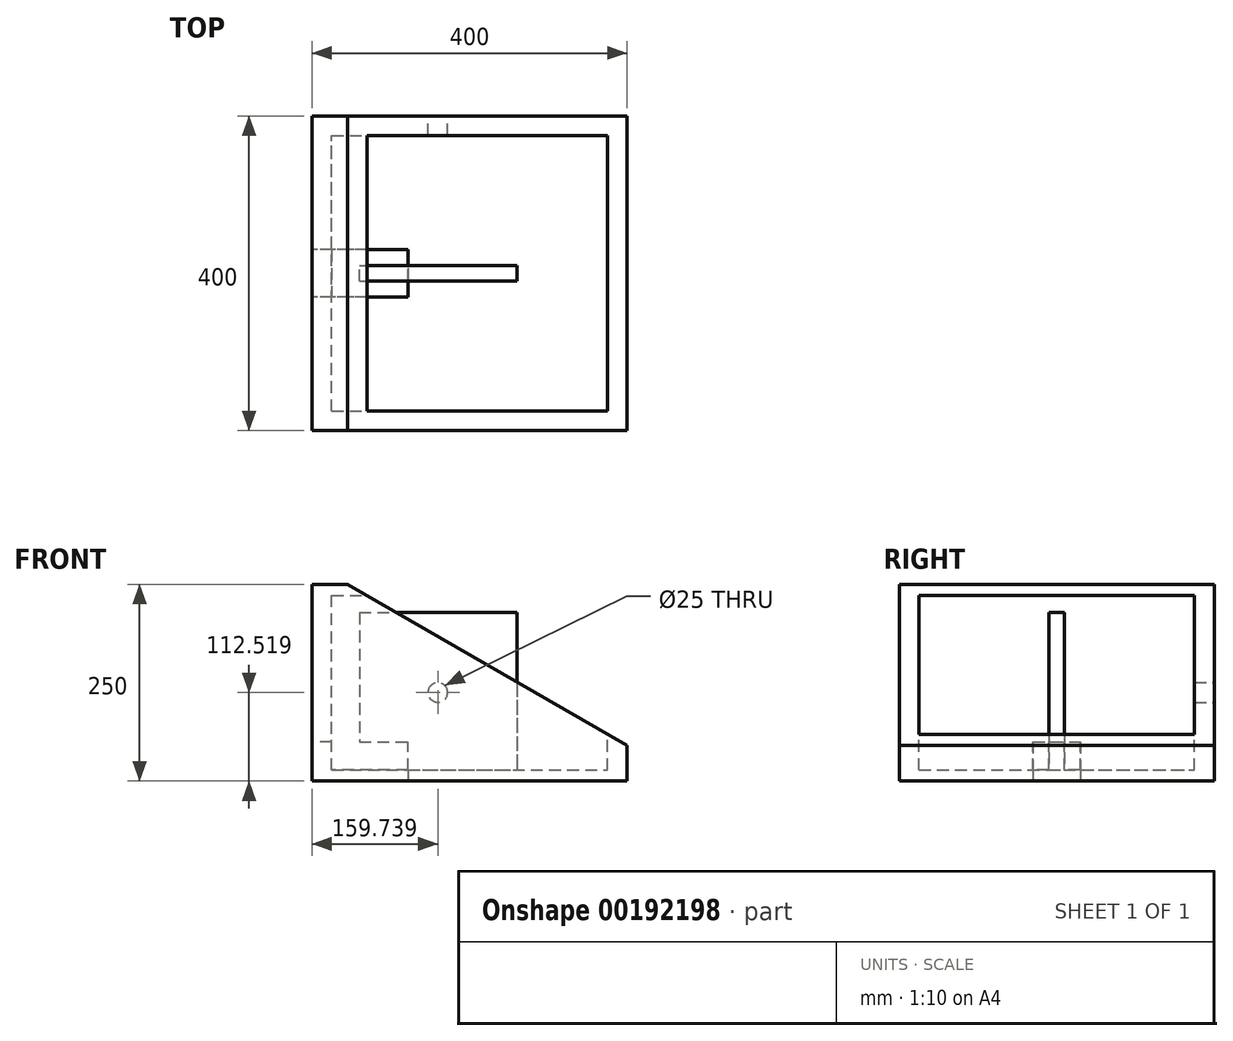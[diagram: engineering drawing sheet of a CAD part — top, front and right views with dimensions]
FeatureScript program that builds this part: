
annotation { "Feature Type Name" : "Feature", "Feature Type Description" : "" }
export const myFeature = defineFeature(function(context is Context, id is Id, definition is map)
    precondition{}
    {
        {
            var Q0;
            Q0=qCreatedBy(makeId("Front.planeOp"),FACE);
            var sketch = newSketch(context, id + "F0", { "sketchPlane" : qUnion([Q0])});
            skLineSegment(sketch, "E0.bottom", {"start": v(-200, -125) * mm, "end": v(200, -125) * mm});
            skLineSegment(sketch, "E0.top", {"start": v(-200, 125) * mm, "end": v(-154.72, 125) * mm});
            skLineSegment(sketch, "E0.left", {"start": v(-200, -125) * mm, "end": v(-200, 125) * mm});
            skLineSegment(sketch, "E0.right", {"start": v(200, -125) * mm, "end": v(200, -79.9) * mm});
            skPoint(sketch, "E0.middle", {"position": v(0, 0) * mm});
            skLineSegment(sketch, "E1", {"start": v(-154.72, 125) * mm, "end": v(200, -79.9) * mm});
            skPoint(sketch, "E2.orphan", {"position": v(200, 125) * mm});
            skSolve(sketch);
        }
        {
            var Q0;
            Q0 = qSketchRegion(id + "F0", true);
            extrude(context, id + "F1", {"entities" : qUnion([Q0]), "depth" : 400 * mm, "symmetric" : true});
        }
        {
            var Q0;
            Q0=qCreatedBy(makeId("Top.planeOp"),FACE);
            var sketch = newSketch(context, id + "F2", { "sketchPlane" : qUnion([Q0])});
            skLineSegment(sketch, "E3.bottom", {"start": v(-175, -175) * mm, "end": v(175, -175) * mm});
            skLineSegment(sketch, "E3.top", {"start": v(-175, 175) * mm, "end": v(175, 175) * mm});
            skLineSegment(sketch, "E3.left", {"start": v(-175, -175) * mm, "end": v(-175, 175) * mm});
            skLineSegment(sketch, "E3.right", {"start": v(175, -175) * mm, "end": v(175, 175) * mm});
            skPoint(sketch, "E3.middle", {"position": v(0, 0) * mm});
            skSolve(sketch);
        }
        {
            var Q0;
            Q0=makeQuery(id+"F2.imprint","IMPRINT",FACE,{"disambiguationData":[TD([[makeQuery(id+"F2.imprint","IMPRINT",EDGE,{"derivedFrom":sQuery(id+"F2.wireOp",EDGE,"E3.bottom")}),1.0]])]});
            extrude(context, id + "F3", {"entities" : qUnion([Q0]), "operationType" : NewBodyOperationType.REMOVE, "oppositeDirection" : true, "depth" : 222 * mm, "symmetric" : true});
        }
        {
            var Q0;
            Q0=makeQuery(id+"F3.boolean.opBoolean","COPY",FACE,{"derivedFrom":makeQuery(id+"F3.opExtrude","CAP_FACE",FACE,{"disambiguationData":[OSD([sQuery(id+"F2.wireOp",EDGE,"E3.bottom"),sQuery(id+"F2.wireOp",EDGE,"E3.top"),sQuery(id+"F2.wireOp",EDGE,"E3.left"),sQuery(id+"F2.wireOp",EDGE,"E3.right")])],"isStart":false})});
            var sketch = newSketch(context, id + "F4", { "sketchPlane" : qUnion([Q0])});
            skLineSegment(sketch, "E4.bottom", {"start": v(-139.94, -10) * mm, "end": v(60.06, -10) * mm});
            skLineSegment(sketch, "E4.top", {"start": v(-139.94, 10) * mm, "end": v(60.06, 10) * mm});
            skLineSegment(sketch, "E4.left", {"start": v(-139.94, -10) * mm, "end": v(-139.94, 10) * mm});
            skLineSegment(sketch, "E4.right", {"start": v(60.06, -10) * mm, "end": v(60.06, 10) * mm});
            skPoint(sketch, "E4.middle", {"position": v(-39.94, 0) * mm});
            skSolve(sketch);
        }
        {
            var Q0;
            Q0=makeQuery(id+"F4.imprint","IMPRINT",FACE,{"disambiguationData":[TD([[makeQuery(id+"F4.imprint","IMPRINT",EDGE,{"derivedFrom":sQuery(id+"F4.wireOp",EDGE,"E4.bottom")}),1.0]])]});
            extrude(context, id + "F5", {"entities" : qUnion([Q0]), "operationType" : NewBodyOperationType.ADD, "depth" : 200 * mm});
        }
        {
            var Q0;
            Q0=makeQuery(id+"F1.opExtrude","CAP_FACE",FACE,{"disambiguationData":[OSD([sQuery(id+"F0.wireOp",EDGE,"E0.bottom"),sQuery(id+"F0.wireOp",EDGE,"E0.top"),sQuery(id+"F0.wireOp",EDGE,"E0.left"),sQuery(id+"F0.wireOp",EDGE,"E0.right"),sQuery(id+"F0.wireOp",EDGE,"E1")])],"isStart":true});
            var sketch = newSketch(context, id + "F6", { "sketchPlane" : qUnion([Q0])});
            skLineSegment(sketch, "E5.bottom", {"start": v(40.26, -12.58) * mm, "end": v(40.26, -12.58) * mm});
            skPoint(sketch, "E5.middle", {"position": v(40.26, -12.48) * mm});
            skCircle(sketch, "E6", {"center": v(40.26, -12.48) * mm, "radius": 12.5 * mm});
            skPoint(sketch, "E7.top.start.orphan", {"position": v(-59.74, -112.48) * mm});
            skPoint(sketch, "E7.right.end.orphan", {"position": v(140.26, -112.48) * mm});
            skPoint(sketch, "E7.bottom.end.orphan", {"position": v(140.26, 87.52) * mm});
            skPoint(sketch, "E7.bottom.start.orphan", {"position": v(-59.74, 87.52) * mm});
            skSolve(sketch);
        }
        {
            var Q0;
            Q0 = qSketchRegion(id + "F6", true);
            extrude(context, id + "F7", {"entities" : qUnion([Q0]), "operationType" : NewBodyOperationType.REMOVE, "oppositeDirection" : true, "depth" : 25 * mm});
        }
        {
            var Q0;
            Q0=makeQuery(id+"F1.opExtrude","SWEPT_FACE",FACE,{"disambiguationData":[OSD([sQuery(id+"F0.wireOp",EDGE,"E0.left")])]});
            var sketch = newSketch(context, id + "F8", { "sketchPlane" : qUnion([Q0])});
            skLineSegment(sketch, "E8.bottom", {"start": v(30, -75) * mm, "end": v(-30, -75) * mm});
            skLineSegment(sketch, "E8.top", {"start": v(30, -175) * mm, "end": v(-30, -175) * mm});
            skLineSegment(sketch, "E8.left", {"start": v(30, -75) * mm, "end": v(30, -175) * mm});
            skLineSegment(sketch, "E8.right", {"start": v(-30, -75) * mm, "end": v(-30, -175) * mm});
            skPoint(sketch, "E8.middle", {"position": v(0, -125) * mm});
            skSolve(sketch);
        }
        {
            var Q0;
            Q0 = qSketchRegion(id + "F8", true);
            extrude(context, id + "F9", {"entities" : qUnion([Q0]), "operationType" : NewBodyOperationType.REMOVE, "oppositeDirection" : true, "depth" : 122 * mm});
        }
    });
